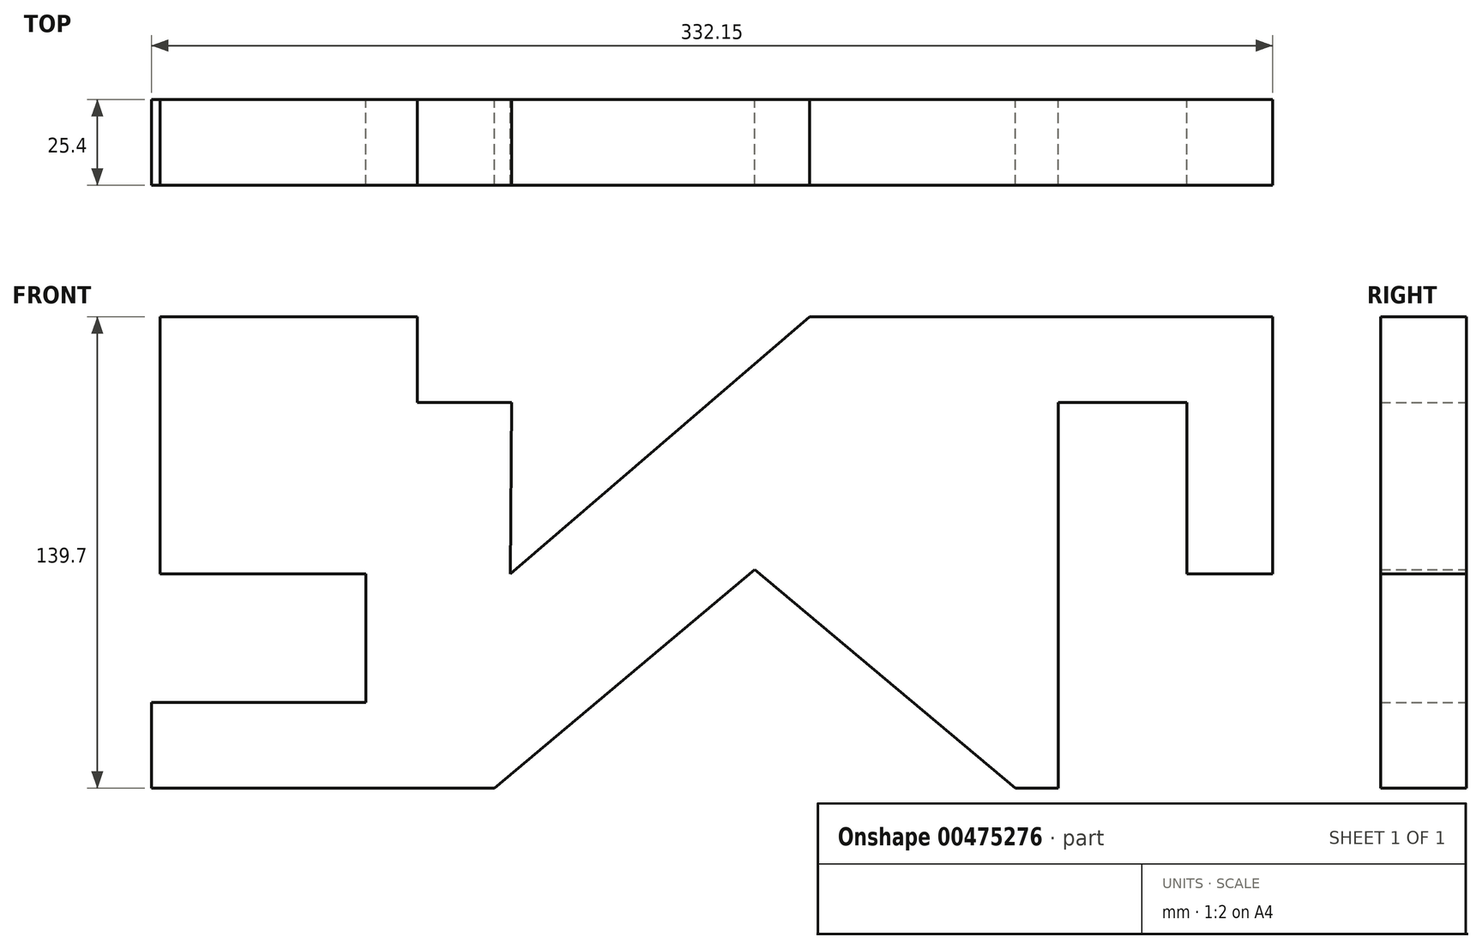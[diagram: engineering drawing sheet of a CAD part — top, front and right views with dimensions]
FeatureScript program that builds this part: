
annotation { "Feature Type Name" : "Feature", "Feature Type Description" : "" }
export const myFeature = defineFeature(function(context is Context, id is Id, definition is map)
    precondition{}
    {
        {
            var Q0;
            Q0=qCreatedBy(makeId("Front.planeOp"),FACE);
            var sketch = newSketch(context, id + "F0", { "sketchPlane" : qUnion([Q0])});
            skLineSegment(sketch, "E0", {"start": v(0, 0) * mm, "end": v(101.6, 0) * mm});
            skLineSegment(sketch, "E1", {"start": v(101.6, 0) * mm, "end": v(178.78, 64.76) * mm});
            skLineSegment(sketch, "E2", {"start": v(178.78, 64.76) * mm, "end": v(255.95, 0) * mm});
            skLineSegment(sketch, "E3", {"start": v(255.95, 0) * mm, "end": v(268.65, 0) * mm});
            skLineSegment(sketch, "E4", {"start": v(268.65, 0) * mm, "end": v(268.65, 114.3) * mm});
            skLineSegment(sketch, "E5", {"start": v(268.65, 114.3) * mm, "end": v(306.75, 114.3) * mm});
            skLineSegment(sketch, "E6", {"start": v(306.75, 114.3) * mm, "end": v(306.75, 63.5) * mm});
            skLineSegment(sketch, "E7", {"start": v(306.75, 63.5) * mm, "end": v(332.15, 63.5) * mm});
            skLineSegment(sketch, "E8", {"start": v(332.15, 63.5) * mm, "end": v(332.15, 139.7) * mm});
            skLineSegment(sketch, "E9", {"start": v(332.15, 139.7) * mm, "end": v(195, 139.7) * mm});
            skLineSegment(sketch, "E10", {"start": v(195, 139.7) * mm, "end": v(106.42, 63.5) * mm});
            skLineSegment(sketch, "E11", {"start": v(106.42, 63.5) * mm, "end": v(106.68, 114.3) * mm});
            skLineSegment(sketch, "E12", {"start": v(106.68, 114.3) * mm, "end": v(78.74, 114.3) * mm});
            skLineSegment(sketch, "E13", {"start": v(78.74, 114.3) * mm, "end": v(78.74, 139.7) * mm});
            skLineSegment(sketch, "E14", {"start": v(78.74, 139.7) * mm, "end": v(2.54, 139.7) * mm});
            skLineSegment(sketch, "E15", {"start": v(2.54, 139.7) * mm, "end": v(2.54, 63.5) * mm});
            skLineSegment(sketch, "E16", {"start": v(2.54, 63.5) * mm, "end": v(63.5, 63.5) * mm});
            skLineSegment(sketch, "E17", {"start": v(63.5, 63.5) * mm, "end": v(63.5, 25.4) * mm});
            skLineSegment(sketch, "E18", {"start": v(63.5, 25.4) * mm, "end": v(0, 25.4) * mm});
            skLineSegment(sketch, "E19", {"start": v(0, 25.4) * mm, "end": v(0, 0) * mm});
            skSolve(sketch);
        }
        {
            var Q0;
            Q0=makeQuery(id+"F0.imprint","IMPRINT",FACE,{"disambiguationData":[TD([[makeQuery(id+"F0.imprint","IMPRINT",EDGE,{"derivedFrom":sQuery(id+"F0.wireOp",EDGE,"E0")}),1.0]])]});
            extrude(context, id + "F1", {"entities" : qUnion([Q0]), "depth" : 25.4 * mm});
        }
    });
